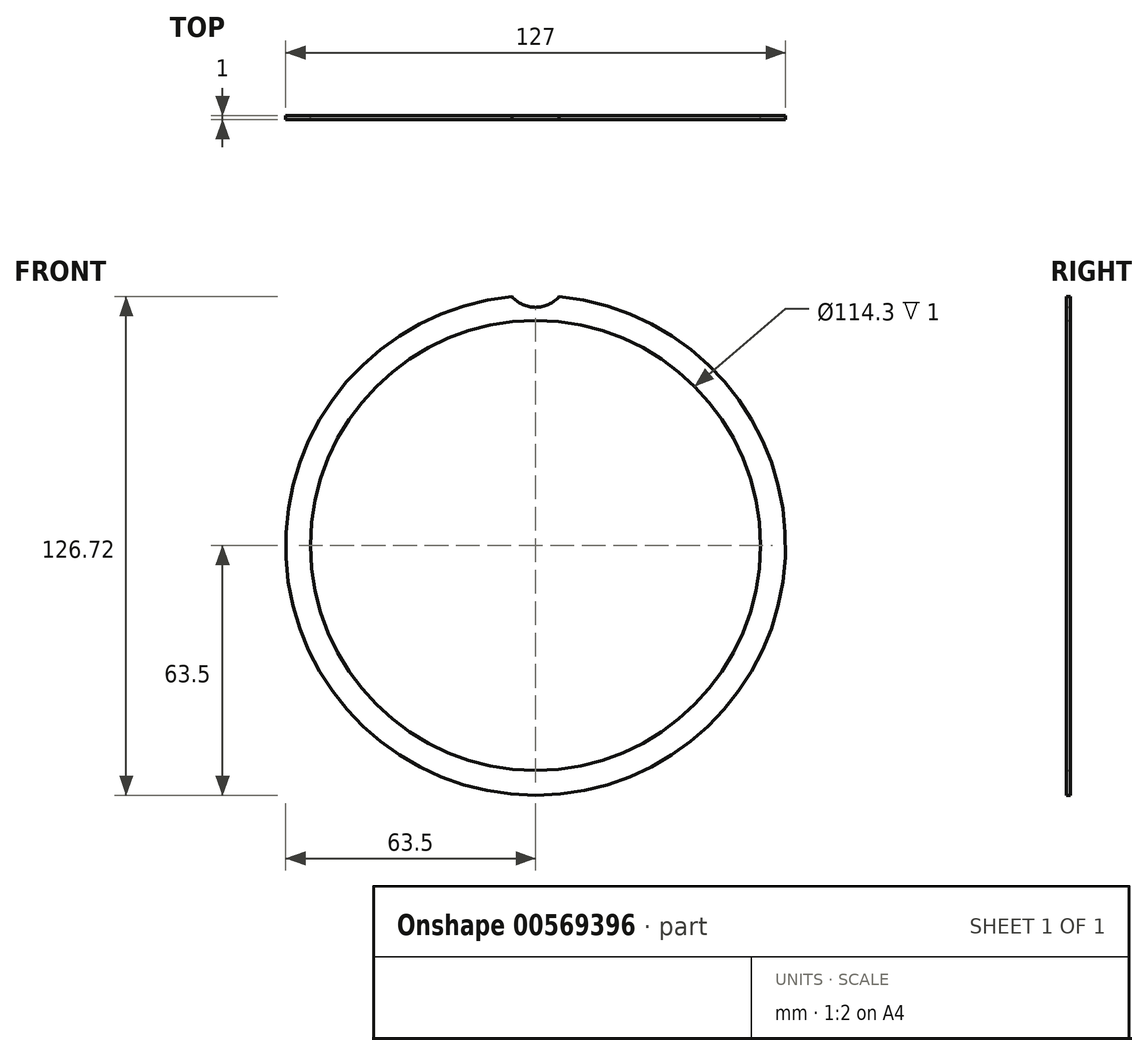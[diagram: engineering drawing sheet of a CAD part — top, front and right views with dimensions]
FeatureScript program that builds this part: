
annotation { "Feature Type Name" : "Feature", "Feature Type Description" : "" }
export const myFeature = defineFeature(function(context is Context, id is Id, definition is map)
    precondition{}
    {
        {
            var Q0;
            Q0=qCreatedBy(makeId("Front.planeOp"),FACE);
            var sketch = newSketch(context, id + "F0", { "sketchPlane" : qUnion([Q0])});
            skCircle(sketch, "E0", {"center": v(0, 0) * mm, "radius": 63.5 * mm});
            skCircle(sketch, "E1", {"center": v(0, 0) * mm, "radius": 57.15 * mm});
            skSolve(sketch);
        }
        {
            var Q0;
            Q0=makeQuery(id+"F0.imprint","IMPRINT",FACE,{"disambiguationData":[TD([[makeQuery(id+"F0.imprint","IMPRINT",EDGE,{"derivedFrom":sQuery(id+"F0.wireOp",EDGE,"E0")}),1.0]])]});
            extrude(context, id + "F1", {"entities" : qUnion([Q0]), "depth" : 1 * mm, "offsetDistance" : 25.4 * mm});
        }
        {
            var Q0;
            Q0=makeQuery(id+"F1.opExtrude","CAP_FACE",FACE,{"disambiguationData":[OSD([sQuery(id+"F0.wireOp",EDGE,"E0"),sQuery(id+"F0.wireOp",EDGE,"E1")])],"isStart":false});
            var sketch = newSketch(context, id + "F2", { "sketchPlane" : qUnion([Q0])});
            skCircle(sketch, "E2", {"center": v(0, 68.47) * mm, "radius": 7.97 * mm});
            skSolve(sketch);
        }
        {
            var Q0;
            {var subQ0=sQuery(id+"F2.wireOp",EDGE,"E2");var subQ1=makeQuery(id+"F1.opExtrude","CAP_EDGE",EDGE,{"disambiguationData":[OSD([sQuery(id+"F0.wireOp",EDGE,"E0")])],"isStart":false});var subQ2=makeQuery(id+"F2.imprint","INTERSECT",VERTEX,{"disambiguationData":[OD(0.0)],"derivedFrom":[subQ1,subQ0]});Q0=makeQuery(id+"F2.imprint","IMPRINT",FACE,{"disambiguationData":[TD([[makeQuery(id+"F2.imprint","IMPRINT",EDGE,{"disambiguationData":[TD([[subQ2,1.0]])],"derivedFrom":subQ0}),1.0]])]});}
            var Q1;
            {var subQ0=sQuery(id+"F2.wireOp",EDGE,"E2");var subQ1=makeQuery(id+"F1.opExtrude","CAP_EDGE",EDGE,{"disambiguationData":[OSD([sQuery(id+"F0.wireOp",EDGE,"E0")])],"isStart":false});var subQ2=makeQuery(id+"F2.imprint","INTERSECT",VERTEX,{"disambiguationData":[OD(0.0)],"derivedFrom":[subQ1,subQ0]});Q1=makeQuery(id+"F2.imprint","IMPRINT",FACE,{"disambiguationData":[TD([[makeQuery(id+"F2.imprint","IMPRINT",EDGE,{"disambiguationData":[TD([[subQ2,-1.0]])],"derivedFrom":subQ0}),1.0]])]});}
            extrude(context, id + "F3", {"entities" : qUnion([Q0, Q1]), "operationType" : NewBodyOperationType.REMOVE, "endBound" : BoundingType.SYMMETRIC, "oppositeDirection" : true, "depth" : 25.4 * mm, "offsetDistance" : 25.4 * mm});
        }
    });
